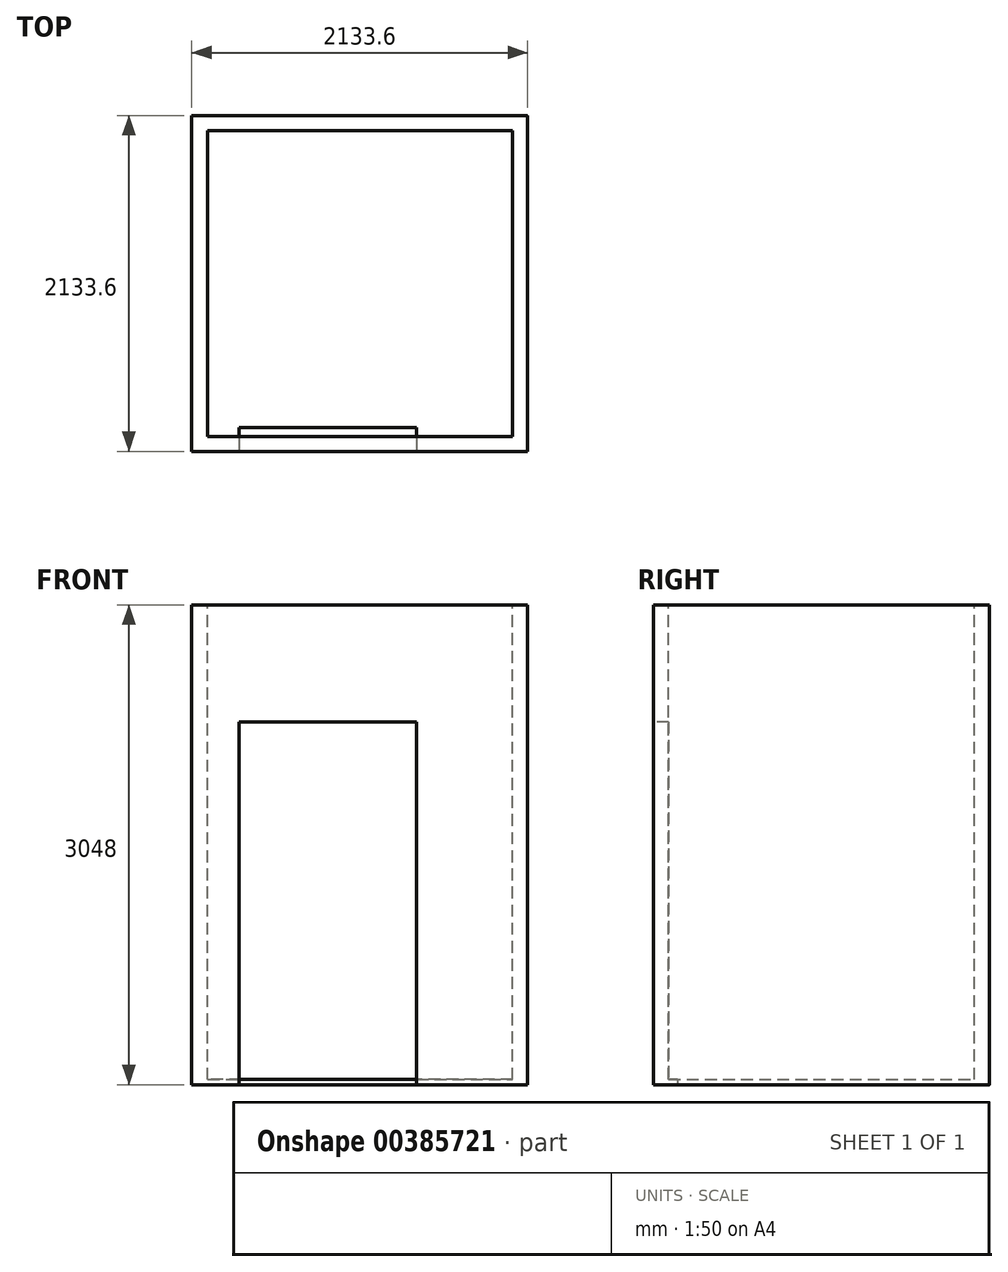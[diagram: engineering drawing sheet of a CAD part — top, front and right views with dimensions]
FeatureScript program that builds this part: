
annotation { "Feature Type Name" : "Feature", "Feature Type Description" : "" }
export const myFeature = defineFeature(function(context is Context, id is Id, definition is map)
    precondition{}
    {
        {
            var Q0;
            Q0=qCreatedBy(makeId("Top.planeOp"),FACE);
            var sketch = newSketch(context, id + "F0", { "sketchPlane" : qUnion([Q0])});
            skLineSegment(sketch, "E0.bottom", {"start": v(1066.8, -1066.8) * mm, "end": v(-1066.8, -1066.8) * mm});
            skLineSegment(sketch, "E0.top", {"start": v(1066.8, 1066.8) * mm, "end": v(-1066.8, 1066.8) * mm});
            skLineSegment(sketch, "E0.left", {"start": v(1066.8, -1066.8) * mm, "end": v(1066.8, 1066.8) * mm});
            skLineSegment(sketch, "E0.right", {"start": v(-1066.8, -1066.8) * mm, "end": v(-1066.8, 1066.8) * mm});
            skPoint(sketch, "E0.middle", {"position": v(0, 0) * mm});
            skSolve(sketch);
        }
        {
            var Q0;
            Q0=makeQuery(id+"F0.imprint","IMPRINT",FACE,{"disambiguationData":[TD([[makeQuery(id+"F0.imprint","IMPRINT",EDGE,{"derivedFrom":sQuery(id+"F0.wireOp",EDGE,"E0.bottom")}),-1.0]])]});
            extrude(context, id + "F1", {"entities" : qUnion([Q0]), "depth" : 3048 * mm});
        }
        {
            var Q0;
            Q0=makeQuery(id+"F1.opExtrude","CAP_FACE",FACE,{"disambiguationData":[OSD([sQuery(id+"F0.wireOp",EDGE,"E0.bottom"),sQuery(id+"F0.wireOp",EDGE,"E0.top"),sQuery(id+"F0.wireOp",EDGE,"E0.left"),sQuery(id+"F0.wireOp",EDGE,"E0.right")])],"isStart":false});
            var sketch = newSketch(context, id + "F2", { "sketchPlane" : qUnion([Q0])});
            skLineSegment(sketch, "E1.0", {"start": v(-965.2, -1066.8) * mm, "end": v(-965.2, 1066.8) * mm});
            skLineSegment(sketch, "E2.0", {"start": v(1073.15, -1073.15) * mm, "end": v(1073.15, 1073.15) * mm});
            skLineSegment(sketch, "E2.1", {"start": v(-1073.15, -1073.15) * mm, "end": v(1073.15, -1073.15) * mm});
            skLineSegment(sketch, "E2.2", {"start": v(-1073.15, 1073.15) * mm, "end": v(-1073.15, -1073.15) * mm});
            skLineSegment(sketch, "E2.3", {"start": v(1073.15, 1073.15) * mm, "end": v(-1073.15, 1073.15) * mm});
            skLineSegment(sketch, "E3.0", {"start": v(971.55, 971.55) * mm, "end": v(-971.55, 971.55) * mm});
            skLineSegment(sketch, "E3.1", {"start": v(971.55, -971.55) * mm, "end": v(971.55, 971.55) * mm});
            skLineSegment(sketch, "E3.2", {"start": v(-971.55, -971.55) * mm, "end": v(971.55, -971.55) * mm});
            skLineSegment(sketch, "E3.3", {"start": v(-971.55, 971.55) * mm, "end": v(-971.55, -971.55) * mm});
            skSolve(sketch);
        }
        {
            var Q0;
            {var subQ5=sQuery(id+"F2.wireOp",EDGE,"E3.1");Q0=makeQuery(id+"F2.imprint","IMPRINT",FACE,{"disambiguationData":[TD([[makeQuery(id+"F2.imprint","IMPRINT",EDGE,{"derivedFrom":subQ5}),1.0]])]});}
            extrude(context, id + "F3", {"entities" : qUnion([Q0]), "operationType" : NewBodyOperationType.REMOVE, "oppositeDirection" : true, "depth" : 2590.8 * mm});
        }
        {
            var Q0;
            Q0=makeQuery(id+"F1.opExtrude","SWEPT_FACE",FACE,{"disambiguationData":[OSD([sQuery(id+"F0.wireOp",EDGE,"E0.bottom")])]});
            var sketch = newSketch(context, id + "F4", { "sketchPlane" : qUnion([Q0])});
            skLineSegment(sketch, "E4.bottom", {"start": v(360.09, 2305.25) * mm, "end": v(-766.8, 2305.25) * mm});
            skLineSegment(sketch, "E4.top", {"start": v(360.09, -2105.04) * mm, "end": v(-766.8, -2105.04) * mm});
            skLineSegment(sketch, "E4.left", {"start": v(360.09, 2305.25) * mm, "end": v(360.09, -2105.04) * mm});
            skLineSegment(sketch, "E4.right", {"start": v(-766.8, 2305.25) * mm, "end": v(-766.8, -2105.04) * mm});
            skPoint(sketch, "E4.middle", {"position": v(-203.36, 100.1) * mm});
            skLineSegment(sketch, "E5.bottom", {"start": v(-85.43, 100.1) * mm, "end": v(-321.29, 100.1) * mm});
            skLineSegment(sketch, "E5.top", {"start": v(-85.43, 100.1) * mm, "end": v(-321.29, 100.1) * mm});
            skLineSegment(sketch, "E5.left", {"start": v(-85.43, 100.1) * mm, "end": v(-85.43, 100.1) * mm});
            skLineSegment(sketch, "E5.right", {"start": v(-321.29, 100.1) * mm, "end": v(-321.29, 100.1) * mm});
            skSolve(sketch);
        }
        {
            var Q0;
            Q0 = qSketchRegion(id + "F4", true);
            extrude(context, id + "F5", {"entities" : qUnion([Q0]), "operationType" : NewBodyOperationType.REMOVE, "oppositeDirection" : true, "depth" : 152.4 * mm});
        }
        {
            var Q0;
            Q0=makeQuery(id+"F3.boolean.opBoolean","COPY",FACE,{"derivedFrom":makeQuery(id+"F3.opExtrude","CAP_FACE",FACE,{"disambiguationData":[OSD([sQuery(id+"F2.wireOp",EDGE,"E1.0"),sQuery(id+"F2.wireOp",EDGE,"E3.0"),sQuery(id+"F2.wireOp",EDGE,"E3.1"),sQuery(id+"F2.wireOp",EDGE,"E3.2")])],"isStart":false})});
            extrude(context, id + "F6", {"entities" : qUnion([Q0]), "operationType" : NewBodyOperationType.REMOVE, "oppositeDirection" : true, "depth" : 424.18 * mm});
        }
        {
            var Q0;
            Q0=makeQuery(id+"F1.opExtrude","SWEPT_EDGE",EDGE,{"disambiguationData":[OSD([sQuery(id+"F0.wireOp",EDGE,"E0.top"),sQuery(id+"F0.wireOp",EDGE,"E0.left")])]});
            fillet(context, id + "F7", {"entities" : qUnion([Q0]), "radius" : 7.62 * mm, "tangentPropagation" : true, "allowEdgeOverflow" : false});
        }
    });
